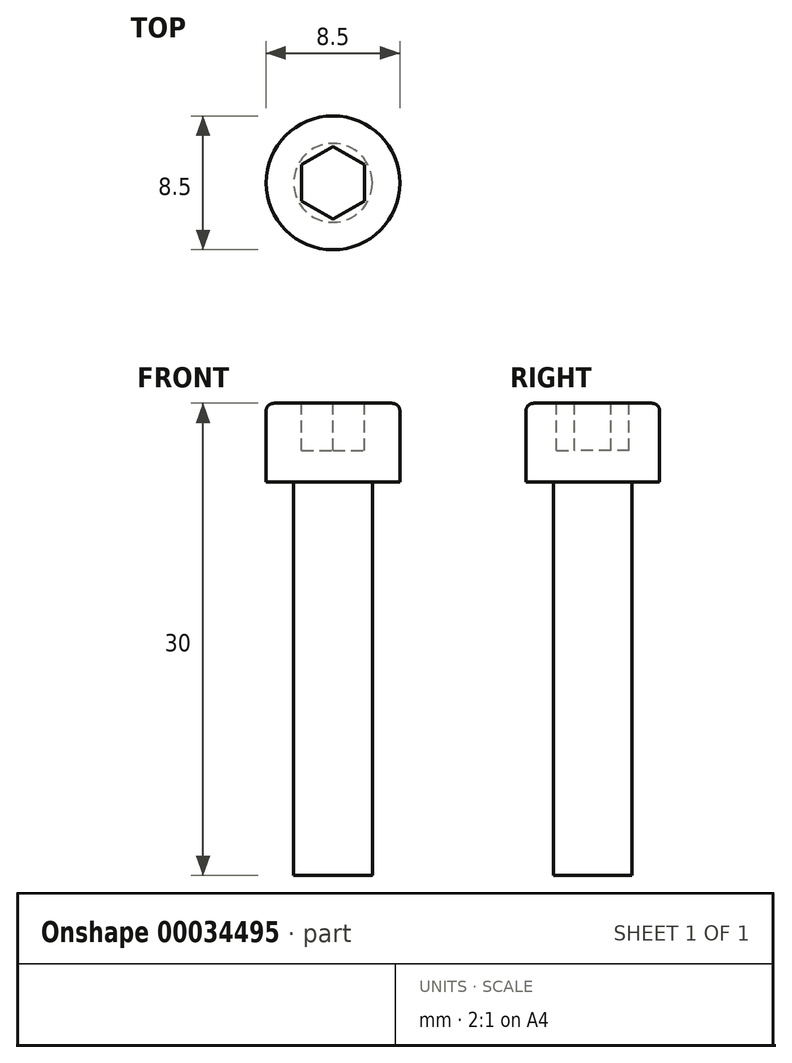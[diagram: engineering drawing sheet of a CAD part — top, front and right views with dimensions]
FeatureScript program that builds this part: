
annotation { "Feature Type Name" : "Feature", "Feature Type Description" : "" }
export const myFeature = defineFeature(function(context is Context, id is Id, definition is map)
    precondition{}
    {
        {
            var Q0;
            Q0=qCreatedBy(makeId("Top.planeOp"),FACE);
            var sketch = newSketch(context, id + "F0", { "sketchPlane" : qUnion([Q0])});
            skCircle(sketch, "E0", {"center": v(0, 0) * mm, "radius": 4.25 * mm});
            skCircle(sketch, "E1", {"center": v(0, 0) * mm, "radius": 2.5 * mm});
            skCircle(sketch, "E2.cCircle", {"center": v(0, 0) * mm, "radius": 2 * mm, "construction": true});
            skLineSegment(sketch, "E2.0", {"start": v(2, 1.15) * mm, "end": v(2, -1.15) * mm});
            skLineSegment(sketch, "E2.1", {"start": v(2, -1.15) * mm, "end": v(0, -2.3) * mm});
            skLineSegment(sketch, "E2.2", {"start": v(0, -2.3) * mm, "end": v(-2, -1.15) * mm});
            skLineSegment(sketch, "E2.3", {"start": v(-2, -1.15) * mm, "end": v(-2, 1.15) * mm});
            skLineSegment(sketch, "E2.4", {"start": v(-2, 1.15) * mm, "end": v(0, 2.3) * mm});
            skLineSegment(sketch, "E2.5", {"start": v(0, 2.3) * mm, "end": v(2, 1.15) * mm});
            skPoint(sketch, "E2.0.midPoint", {"position": v(2, 0) * mm});
            skSolve(sketch);
        }
        {
            var Q0;
            Q0 = qSketchRegion(id + "F0", true);
            extrude(context, id + "F1", {"entities" : qUnion([Q0]), "oppositeDirection" : true, "depth" : 5 * mm});
        }
        {
            var Q0;
            Q0=makeQuery(id+"F0.imprint","IMPRINT",FACE,{"disambiguationData":[TD([[makeQuery(id+"F0.imprint","IMPRINT",EDGE,{"derivedFrom":sQuery(id+"F0.wireOp",EDGE,"E1")}),1.0]])]});
            var Q1;
            Q1=makeQuery(id+"F0.imprint","IMPRINT",FACE,{"disambiguationData":[TD([[makeQuery(id+"F0.imprint","IMPRINT",EDGE,{"derivedFrom":sQuery(id+"F0.wireOp",EDGE,"E2.0")}),-1.0]])]});
            extrude(context, id + "F2", {"entities" : qUnion([Q0, Q1]), "operationType" : NewBodyOperationType.ADD, "oppositeDirection" : true, "depth" : 30 * mm});
        }
        {
            var Q0;
            Q0=makeQuery(id+"F0.imprint","IMPRINT",FACE,{"disambiguationData":[TD([[makeQuery(id+"F0.imprint","IMPRINT",EDGE,{"derivedFrom":sQuery(id+"F0.wireOp",EDGE,"E2.0")}),-1.0]])]});
            extrude(context, id + "F3", {"entities" : qUnion([Q0]), "operationType" : NewBodyOperationType.REMOVE, "oppositeDirection" : true, "depth" : 3 * mm});
        }
        {
            var Q0;
            Q0=makeQuery(id+"F1.opExtrude","CAP_EDGE",EDGE,{"disambiguationData":[OSD([sQuery(id+"F0.wireOp",EDGE,"E0")])],"isStart":true});
            fillet(context, id + "F4", {"entities" : qUnion([Q0]), "radius" : 0.5 * mm, "tangentPropagation" : true, "allowEdgeOverflow" : false});
        }
    });
